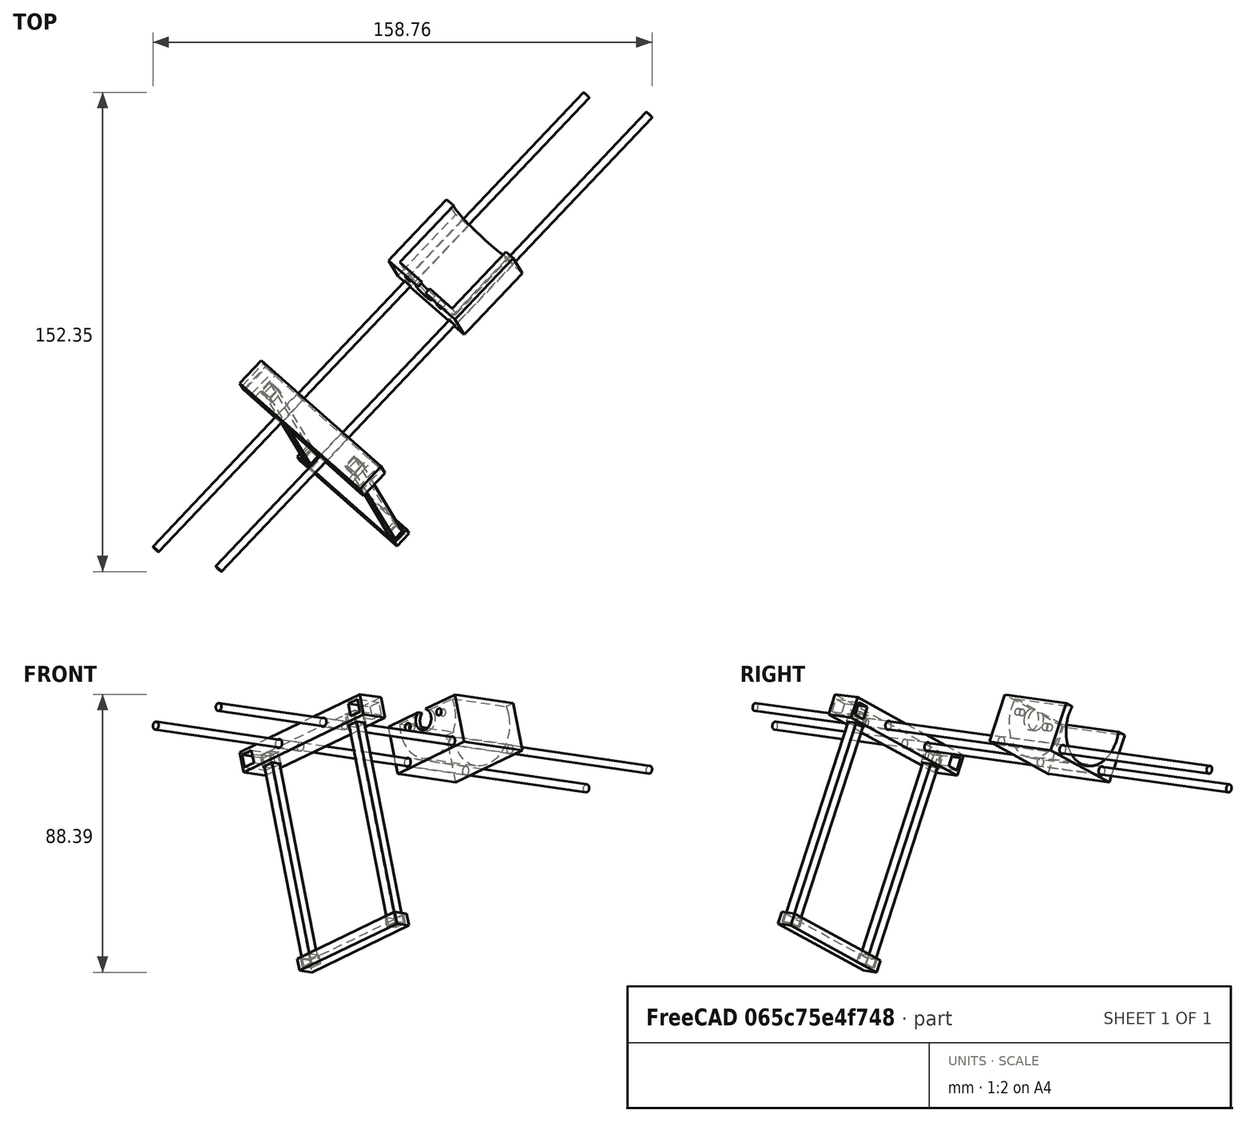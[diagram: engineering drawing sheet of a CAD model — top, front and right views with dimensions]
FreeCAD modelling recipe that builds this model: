
FCSTD DOCUMENT  (FreeCAD 0.19R24366 (Git))
Label: sailface_assembly_v1
License: All rights reserved
LicenseURL: http://en.wikipedia.org/wiki/All_rights_reserved
objects: Part::FeaturePython×53, App::FeaturePython×25, App::Link×10, App::MeasureDistance×1
note: 51 computed .brp shape members not serialized (recipe doc carries the construction recipe); baked Part::Feature solids carry a one-line shape summary decoded from their .brp
EXTERNAL_REF file=rudder_coarse_1.FCStd obj=Part
EXTERNAL_REF file=hulltest9.FCStd obj=Part
EXTERNAL_REF file=ServoSunFinderSF3218MG.FCStd obj=Part
EXTERNAL_REF file=Battery_VoltaicV70.FCStd obj=Part
EXTERNAL_REF file=internalstructure.FCStd obj=Assembly001
EXTERNAL_REF file=sailface_prop_motor_assembly.FCStd obj=Assembly001
EXTERNAL_REF file=ElectronicAssembly.FCStd obj=Part003

FEATURE [App::Link] Link  label="PartRudderWithPost"
  LinkPlacement = pos=(-220.039,-29.8961,-114.206) rot=(0.968596,0.172423,0.179146;1.79451rad)
  LinkedObject = -> <external rudder_coarse_1.FCStd>#Part
  Placement = pos=(-220.039,-29.8961,-114.206) rot=(0.968596,0.172423,0.179146;1.79451rad)
FEATURE [App::Link] Link002  label="Hull9"
  LinkPlacement = pos=(159.25,63.0194,-342.139) rot=(0.956231,-0.262504,0.12928;2.88979rad)
  LinkedObject = -> <external hulltest9.FCStd>#Part
  Placement = pos=(159.25,63.0194,-342.139) rot=(0.956231,-0.262504,0.12928;2.88979rad)
FEATURE [App::Link] Link003  label="Servo_SF3218MG001"
  LinkPlacement = pos=(50.6845,245.566,-385.314) rot=(0.448667,0.484449,-0.751004;2.6409rad)
  LinkedObject = -> <external ServoSunFinderSF3218MG.FCStd>#Part
  Placement = pos=(50.6845,245.566,-385.314) rot=(0.448667,0.484449,-0.751004;2.6409rad)
FEATURE [App::Link] Link012  label="PartBatteryVoltaicV071"
  LinkPlacement = pos=(257.834,77.0747,-229.776) rot=(0.318237,-0.762093,0.563861;1.78727rad)
  LinkedObject = -> <external Battery_VoltaicV70.FCStd>#Part
  Placement = pos=(257.834,77.0747,-229.776) rot=(0.318237,-0.762093,0.563861;1.78727rad)
FEATURE [App::Link] Link013  label="InternalHolder"
  LinkPlacement = pos=(53.3906,223.534,-322.627) rot=(-0.671245,-0.121056,-0.731283;2.04659rad)
  LinkedObject = -> <external internalstructure.FCStd>#Assembly001
  Placement = pos=(53.3906,223.534,-322.627) rot=(-0.671245,-0.121056,-0.731283;2.04659rad)
FEATURE [Part::FeaturePython] Parts  # WARN: FeaturePython — macro-defined, semantics opaque (R4)
  Group = -> [Link,Link003,Link013]
  GroupMode = 0
FEATURE [App::Link] Link015  label="InternalHolder001"
  LinkPlacement = pos=(36.7501,244.979,-385.283) rot=(0.56648,0.820791,0.073504;1.79616rad)
  LinkedObject = -> <external internalstructure.FCStd>#Assembly001
  Placement = pos=(36.7501,244.979,-385.283) rot=(0.56648,0.820791,0.073504;1.79616rad)
FEATURE [App::Link] Link016  label="PropMotorAssembly001"
  LinkPlacement = pos=(-323.878,337.344,47.3147) rot=(-0.16827,-0.265613,-0.949281;1.40405rad)
  LinkedObject = -> <external sailface_prop_motor_assembly.FCStd>#Assembly001
  Placement = pos=(-323.878,337.344,47.3147) rot=(-0.16827,-0.265613,-0.949281;1.40405rad)
FEATURE [App::Link] Link017  label="Servo_SF3218MG002"
  LinkPlacement = pos=(69.9259,133.783,-332.457) rot=(0.343106,0.929153,-0.137671;2.95548rad)
  LinkedObject = -> <external ServoSunFinderSF3218MG.FCStd>#Part
  Placement = pos=(69.9259,133.783,-332.457) rot=(0.343106,0.929153,-0.137671;2.95548rad)
FEATURE [App::Link] Link018  label="PartRudderWithPost001"
  LinkPlacement = pos=(-10.9166,185.291,-322.393) rot=(-0.886207,0.1344,-0.443367;1.71414rad)
  LinkedObject = -> <external rudder_coarse_1.FCStd>#Part
  Placement = pos=(-10.9166,185.291,-322.393) rot=(-0.886207,0.1344,-0.443367;1.71414rad)
FEATURE [App::MeasureDistance] Distance  label="Distance: 87.01 mm"
  Distance = 87.0115
  P1 = (104.997,143.854,-281.372)
  P2 = (50.1048,77.3799,-293.166)
FEATURE [App::Link] Link019  label="ElectronicsEnclosure"
  LinkedObject = -> <external ElectronicAssembly.FCStd>#Part003
FEATURE [Part::FeaturePython] Parts002  label="MasterAssemblyParts"  # WARN: FeaturePython — macro-defined, semantics opaque (R4)
  Group = -> [Link002,Link012,Link015,Link016,Link017,Link018,Link019]
  GroupMode = 0
FEATURE [Part::FeaturePython] Assembly  # WARN: FeaturePython — macro-defined, semantics opaque (R4)
  AutoRelax = true
  BuildShape = 0
  Freeze = true
  Group = -> [Constraints,Elements,Parts]
  Verbose = false
  _SolverType = 1
  _Version = 1
FEATURE [App::FeaturePython] Constraints  # WARN: FeaturePython — macro-defined, semantics opaque (R4)
  Group = -> [Constraint,Constraint006]
  _Version = 1
FEATURE [App::FeaturePython] Elements  # WARN: FeaturePython — macro-defined, semantics opaque (R4)
  Group = -> [_Element001,_Element003,_Element005,_Element008,_Element011,_Element012,_Element,_Element013,_Element014,_Element015,_Element016,_Element017,_Element018,_Element019,_Element020,_Element023,_Element025,_Element027,_Element029,_Element034,_Element035,_Element040,_Element041,_Element042]
FEATURE [Part::FeaturePython] _Element001  # link proxy (typed FeaturePython)
  Detach = false
  LinkTransform = true
  LinkedObject = -> Link002 [Extrude011.Face10]
  _Parent = -> Elements
FEATURE [Part::FeaturePython] _Element003  # link proxy (typed FeaturePython)
  Detach = false
  LinkTransform = true
  LinkedObject = -> Link002 [Extrude011.Face4]
  _Parent = -> Elements
FEATURE [Part::FeaturePython] _Element005  # link proxy (typed FeaturePython)
  Detach = false
  LinkTransform = true
  LinkedObject = -> Link002 [Extrude011.Face6]
  _Parent = -> Elements
FEATURE [Part::FeaturePython] _Element008  # link proxy (typed FeaturePython)
  Detach = false
  LinkTransform = true
  LinkedObject = -> Link003 [Solid.Face33]
  _Parent = -> Elements
FEATURE [Part::FeaturePython] _Element011  # link proxy (typed FeaturePython)
  Detach = false
  LinkTransform = true
  LinkedObject = -> Link003 [Solid.Face34]
  _Parent = -> Elements
FEATURE [Part::FeaturePython] _Element012  # link proxy (typed FeaturePython)
  Detach = false
  LinkTransform = true
  LinkedObject = -> Link003 [Solid.Face1]
  _Parent = -> Elements
FEATURE [Part::FeaturePython] _Element  # link proxy (typed FeaturePython)
  Detach = false
  LinkTransform = true
  LinkedObject = -> Link013 [1.$Element.]
  _Parent = -> Elements
FEATURE [Part::FeaturePython] _Element013  # link proxy (typed FeaturePython)
  Detach = false
  LinkTransform = true
  LinkedObject = -> Link012 [Pad001.Face2]
  _Parent = -> Elements
FEATURE [Part::FeaturePython] _Element014  # link proxy (typed FeaturePython)
  Detach = false
  LinkTransform = true
  LinkedObject = -> Link012 [Pad001.Face5]
  _Parent = -> Elements
FEATURE [Part::FeaturePython] _Element015  # link proxy (typed FeaturePython)
  Detach = false
  LinkTransform = true
  LinkedObject = -> Link013 [1.$Element001.]
  _Parent = -> Elements
FEATURE [App::FeaturePython] Constraint  label="PlaneAlignment001"  # WARN: FeaturePython — macro-defined, semantics opaque (R4)
  Angle = 0
  AnglePitch = 0
  AngleRoll = 0
  Cascade = false
  Disabled = false
  Group = -> [ElementLink,ElementLink011]
  LockAngle = false
  _ConstraintType = 37
  _Parent = -> Constraints
FEATURE [App::FeaturePython] ElementLink  label="_Element014"  # link proxy (typed FeaturePython)
  LinkTransform = true
  LinkedObject = -> _Element014
  _Parent = -> Constraint
FEATURE [App::FeaturePython] ElementLink011  label="_Element015"  # link proxy (typed FeaturePython)
  LinkTransform = true
  LinkedObject = -> _Element015
  _Parent = -> Constraint
FEATURE [Part::FeaturePython] _Element016  # link proxy (typed FeaturePython)
  Detach = false
  LinkTransform = true
  LinkedObject = -> Link013 [1.$Element002.]
  _Parent = -> Elements
FEATURE [Part::FeaturePython] _Element017  # link proxy (typed FeaturePython)
  Detach = false
  LinkTransform = true
  LinkedObject = -> Link013 [1.$Element003.]
  _Parent = -> Elements
FEATURE [Part::FeaturePython] _Element018  # link proxy (typed FeaturePython)
  Detach = false
  LinkTransform = true
  LinkedObject = -> Link013 [1.$Element004.]
  _Parent = -> Elements
FEATURE [Part::FeaturePython] _Element019  # link proxy (typed FeaturePython)
  Detach = false
  LinkTransform = true
  LinkedObject = -> Link003 [Solid.Face107]
  _Parent = -> Elements
FEATURE [App::FeaturePython] Constraint006  label="PlaneCoincident001"  # WARN: FeaturePython — macro-defined, semantics opaque (R4)
  Angle = 0
  AnglePitch = 0
  AngleRoll = 0
  Cascade = false
  Disabled = false
  Group = -> [ElementLink014,ElementLink015]
  LockAngle = false
  Multiply = false
  OffsetX = 0
  OffsetY = 0
  _ConstraintType = 35
  _Parent = -> Constraints
FEATURE [App::FeaturePython] ElementLink014  label="_Element012"  # link proxy (typed FeaturePython)
  LinkTransform = true
  LinkedObject = -> _Element012
  _Parent = -> Constraint006
FEATURE [App::FeaturePython] ElementLink015  label="_Element017"  # link proxy (typed FeaturePython)
  LinkTransform = true
  LinkedObject = -> _Element017
  _Parent = -> Constraint006
FEATURE [Part::FeaturePython] _Element020  # link proxy (typed FeaturePython)
  Detach = false
  LinkTransform = true
  LinkedObject = -> Link013 [1.$Element005.]
  _Parent = -> Elements
FEATURE [Part::FeaturePython] _Element023  # link proxy (typed FeaturePython)
  Detach = false
  LinkTransform = true
  LinkedObject = -> Link013 [1.$Element006.]
  _Parent = -> Elements
FEATURE [Part::FeaturePython] _Element025  # link proxy (typed FeaturePython)
  Detach = false
  LinkTransform = true
  LinkedObject = -> Link013 [1.$Element007.]
  _Parent = -> Elements
FEATURE [Part::FeaturePython] _Element027  # link proxy (typed FeaturePython)
  Detach = false
  LinkTransform = true
  LinkedObject = -> Link013 [1.$Element008.]
  _Parent = -> Elements
FEATURE [Part::FeaturePython] _Element029  # link proxy (typed FeaturePython)
  Detach = false
  LinkTransform = true
  LinkedObject = -> Link013 [1.$Element009.]
  _Parent = -> Elements
FEATURE [Part::FeaturePython] _Element034  # link proxy (typed FeaturePython)
  Detach = false
  LinkTransform = true
  LinkedObject = -> Link013 [1.$Element010.]
  _Parent = -> Elements
FEATURE [Part::FeaturePython] _Element035  # link proxy (typed FeaturePython)
  Detach = false
  LinkTransform = true
  LinkedObject = -> Link013 [1.$Element011.]
  _Parent = -> Elements
FEATURE [Part::FeaturePython] _Element040  # link proxy (typed FeaturePython)
  Detach = false
  LinkTransform = true
  LinkedObject = -> Link013 [1.$_Element061.]
  _Parent = -> Elements
FEATURE [Part::FeaturePython] _Element041  # link proxy (typed FeaturePython)
  Detach = false
  LinkTransform = true
  LinkedObject = -> Link002 [Compound.Face4]
  _Parent = -> Elements
FEATURE [Part::FeaturePython] _Element042  # link proxy (typed FeaturePython)
  Detach = false
  LinkTransform = true
  LinkedObject = -> Link013 [1.$Element012.]
  _Parent = -> Elements
FEATURE [Part::FeaturePython] Assembly002  label="MasterAssembly"  # WARN: FeaturePython — macro-defined, semantics opaque (R4)
  AutoRelax = true
  BuildShape = 0
  Freeze = false
  Group = -> [Constraints002,Elements002,Parts002]
  Verbose = false
  _SolverType = 1
  _Version = 1
FEATURE [App::FeaturePython] Constraints002  # WARN: FeaturePython — macro-defined, semantics opaque (R4)
  Group = -> [Constraint007,Constraint008,Constraint009,Constraint010,Constraint011]
  _Version = 1
FEATURE [App::FeaturePython] Elements002  label="MasterAssemblyElements"  # WARN: FeaturePython — macro-defined, semantics opaque (R4)
  Group = -> [_Element043,_Element044,_Element045,_Element046,_Element047,_Element048,_Element049,_Element050,_Element051,_Element052,_Element053,_Element054,_Element055,_Element056,_Element057,_Element058,_Element059,_Element060,_Element061,_Element062,_Element063,_Element064,_Element065,_Element066,_Element067]
FEATURE [Part::FeaturePython] _Element043  # link proxy (typed FeaturePython)
  Detach = false
  LinkTransform = true
  LinkedObject = -> Link015 [1.$Element013.]
  _Parent = -> Elements002
FEATURE [Part::FeaturePython] _Element044  # link proxy (typed FeaturePython)
  Detach = false
  LinkTransform = true
  LinkedObject = -> Link002 [Extrude011.Face18]
  _Parent = -> Elements002
FEATURE [Part::FeaturePython] _Element045  # link proxy (typed FeaturePython)
  Detach = false
  LinkTransform = true
  LinkedObject = -> Link015 [1.$_Element064.]
  _Parent = -> Elements002
FEATURE [Part::FeaturePython] _Element046  # link proxy (typed FeaturePython)
  Detach = false
  LinkTransform = true
  LinkedObject = -> Link002 [Compound.Face4]
  _Parent = -> Elements002
FEATURE [App::FeaturePython] Constraint007  label="PlaneCoincident"  # WARN: FeaturePython — macro-defined, semantics opaque (R4)
  Angle = 0
  AnglePitch = 0
  AngleRoll = 0
  Cascade = false
  Disabled = false
  Group = -> [ElementLink016,ElementLink017]
  LockAngle = false
  Multiply = false
  OffsetX = 0
  OffsetY = 0
  _ConstraintType = 35
  _Parent = -> Constraints002
FEATURE [App::FeaturePython] ElementLink016  label="_Element043"  # link proxy (typed FeaturePython)
  LinkTransform = true
  LinkedObject = -> _Element043
  _Parent = -> Constraint007
FEATURE [App::FeaturePython] ElementLink017  label="_Element044"  # link proxy (typed FeaturePython)
  LinkTransform = true
  LinkedObject = -> _Element044
  _Parent = -> Constraint007
FEATURE [Part::FeaturePython] _Element047  # link proxy (typed FeaturePython)
  Detach = false
  LinkTransform = true
  LinkedObject = -> Link015 [1.$Element014.]
  _Parent = -> Elements002
FEATURE [Part::FeaturePython] _Element048  # link proxy (typed FeaturePython)
  Detach = false
  LinkTransform = true
  LinkedObject = -> Link015 [1.$Element015.]
  _Parent = -> Elements002
FEATURE [Part::FeaturePython] _Element049  # link proxy (typed FeaturePython)
  Detach = false
  LinkTransform = true
  LinkedObject = -> Link015 [1.$Element011.]
  _Parent = -> Elements002
FEATURE [Part::FeaturePython] _Element050  # link proxy (typed FeaturePython)
  Detach = false
  LinkTransform = true
  LinkedObject = -> Link015 [1.$Element016.]
  _Parent = -> Elements002
FEATURE [Part::FeaturePython] _Element051  # link proxy (typed FeaturePython)
  Detach = false
  LinkTransform = true
  LinkedObject = -> Link016 [1.$Element.]
  _Parent = -> Elements002
FEATURE [Part::FeaturePython] _Element052  # link proxy (typed FeaturePython)
  Detach = false
  LinkTransform = true
  LinkedObject = -> Link015 [1.$Element006.]
  _Parent = -> Elements002
FEATURE [Part::FeaturePython] _Element053  # link proxy (typed FeaturePython)
  Detach = false
  LinkTransform = true
  LinkedObject = -> Link016 [1.$Element001.]
  _Parent = -> Elements002
FEATURE [Part::FeaturePython] _Element054  # link proxy (typed FeaturePython)
  Detach = false
  LinkTransform = true
  LinkedObject = -> Link015 [1.$Element007.]
  _Parent = -> Elements002
FEATURE [Part::FeaturePython] _Element055  # link proxy (typed FeaturePython)
  Detach = false
  LinkTransform = true
  LinkedObject = -> Link016 [1.$Element002.]
  _Parent = -> Elements002
FEATURE [Part::FeaturePython] _Element056  # link proxy (typed FeaturePython)
  Detach = false
  LinkTransform = true
  LinkedObject = -> Link016 [1.$Element003.]
  _Parent = -> Elements002
FEATURE [Part::FeaturePython] _Element057  # link proxy (typed FeaturePython)
  Detach = false
  LinkTransform = true
  LinkedObject = -> Link015 [1.$Element008.]
  _Parent = -> Elements002
FEATURE [Part::FeaturePython] _Element058  # link proxy (typed FeaturePython)
  Detach = false
  LinkTransform = true
  LinkedObject = -> Link016 [1.$Element004.]
  _Parent = -> Elements002
FEATURE [Part::FeaturePython] _Element059  # link proxy (typed FeaturePython)
  Detach = false
  LinkTransform = true
  LinkedObject = -> Link015 [1.$Element009.]
  _Parent = -> Elements002
FEATURE [App::FeaturePython] Constraint008  label="AxialAlignment"  # WARN: FeaturePython — macro-defined, semantics opaque (R4)
  Angle = 0
  AnglePitch = 0
  AngleRoll = 0
  Disabled = false
  Group = -> [ElementLink018,ElementLink019]
  LockAngle = false
  Multiply = false
  _ConstraintType = 36
  _Parent = -> Constraints002
FEATURE [App::FeaturePython] ElementLink018  label="_Element052"  # link proxy (typed FeaturePython)
  LinkTransform = true
  LinkedObject = -> _Element052
  _Parent = -> Constraint008
FEATURE [App::FeaturePython] ElementLink019  label="_Element051"  # link proxy (typed FeaturePython)
  LinkTransform = true
  LinkedObject = -> _Element051
  _Parent = -> Constraint008
FEATURE [Part::FeaturePython] _Element060  # link proxy (typed FeaturePython)
  Detach = false
  LinkTransform = true
  LinkedObject = -> Link015 [1.$Element017.]
  _Parent = -> Elements002
FEATURE [Part::FeaturePython] _Element061  # link proxy (typed FeaturePython)
  Detach = false
  LinkTransform = true
  LinkedObject = -> Link012 [Pad001.Face2]
  _Parent = -> Elements002
FEATURE [Part::FeaturePython] _Element062  # link proxy (typed FeaturePython)
  Detach = false
  LinkTransform = true
  LinkedObject = -> Link015 [1.$Element001.]
  _Parent = -> Elements002
FEATURE [Part::FeaturePython] _Element063  # link proxy (typed FeaturePython)
  Detach = false
  LinkTransform = true
  LinkedObject = -> Link012 [Pad001.Face4]
  _Parent = -> Elements002
FEATURE [Part::FeaturePython] _Element064  # link proxy (typed FeaturePython)
  Detach = false
  LinkTransform = true
  LinkedObject = -> Link012 [Pad001.Face1]
  _Parent = -> Elements002
FEATURE [Part::FeaturePython] _Element065  # link proxy (typed FeaturePython)
  Detach = false
  LinkTransform = true
  LinkedObject = -> Link015 [1.$Element018.]
  _Parent = -> Elements002
FEATURE [Part::FeaturePython] _Element066  # link proxy (typed FeaturePython)
  Detach = false
  LinkTransform = true
  LinkedObject = -> Link012 [Pad001.Face3]
  _Parent = -> Elements002
FEATURE [Part::FeaturePython] _Element067  # link proxy (typed FeaturePython)
  Detach = false
  LinkTransform = true
  LinkedObject = -> Link015 [1.$Element.]
  _Parent = -> Elements002
FEATURE [App::FeaturePython] Constraint009  label="MultiParallel"  # WARN: FeaturePython — macro-defined, semantics opaque (R4)
  Angle = 0
  AnglePitch = 0
  AngleRoll = 0
  Disabled = false
  Group = -> [ElementLink020,ElementLink021]
  LockAngle = false
  _ConstraintType = 291
  _Parent = -> Constraints002
FEATURE [App::FeaturePython] ElementLink020  label="_Element061"  # link proxy (typed FeaturePython)
  LinkTransform = true
  LinkedObject = -> _Element061
  _Parent = -> Constraint009
FEATURE [App::FeaturePython] ElementLink021  label="_Element060"  # link proxy (typed FeaturePython)
  LinkTransform = true
  LinkedObject = -> _Element060
  _Parent = -> Constraint009
FEATURE [App::FeaturePython] Constraint010  label="PlaneAlignment"  # WARN: FeaturePython — macro-defined, semantics opaque (R4)
  Angle = 0
  AnglePitch = 0
  AngleRoll = 0
  Cascade = false
  Disabled = false
  Group = -> [ElementLink022,ElementLink023]
  LockAngle = false
  _ConstraintType = 37
  _Parent = -> Constraints002
FEATURE [App::FeaturePython] ElementLink022  label="_Element064"  # link proxy (typed FeaturePython)
  LinkTransform = true
  LinkedObject = -> _Element064
  _Parent = -> Constraint010
FEATURE [App::FeaturePython] ElementLink023  label="_Element065"  # link proxy (typed FeaturePython)
  LinkTransform = true
  LinkedObject = -> _Element065
  _Parent = -> Constraint010
FEATURE [App::FeaturePython] Constraint011  label="PlaneAlignment002"  # WARN: FeaturePython — macro-defined, semantics opaque (R4)
  Angle = 0
  AnglePitch = 0
  AngleRoll = 0
  Cascade = false
  Disabled = false
  Group = -> [ElementLink024,ElementLink025]
  LockAngle = false
  _ConstraintType = 37
  _Parent = -> Constraints002
FEATURE [App::FeaturePython] ElementLink024  label="_Element063"  # link proxy (typed FeaturePython)
  LinkTransform = true
  LinkedObject = -> _Element063
  _Parent = -> Constraint011
FEATURE [App::FeaturePython] ElementLink025  label="_Element062"  # link proxy (typed FeaturePython)
  LinkTransform = true
  LinkedObject = -> _Element062
  _Parent = -> Constraint011

RESOLVED EXTERNAL PARTS (link-assembly join: the EXTERNAL_REF files above that resolve inside this repo's crawl, each included once):
---- part ServoSunFinderSF3218MG.FCStd = doc fcstd_3688cb63020c ----
FCSTD DOCUMENT  (FreeCAD 0.19R24366 (Git))
Label: ServoSunFinderSF3218MG
License: All rights reserved
LicenseURL: http://en.wikipedia.org/wiki/All_rights_reserved
objects: Sketcher::SketchObject×15, PartDesign::Pad×10, PartDesign::Pocket×5, App::Part×5, PartDesign::Body×4, Part::Feature×2, Mesh::Feature×1
note: 51 computed .brp shape members not serialized (recipe doc carries the construction recipe); baked Part::Feature solids carry a one-line shape summary decoded from their .brp

FEATURE [Part::Feature] Solid  label="Servo_SF3218MG"
  Placement = pos=(0,0,0) rot=(1,0,0;1.5708rad)
  shape: bbox 20 x 62.45 x 46.03 mm, 436 faces (baked)
FEATURE [Sketcher::SketchObject] Sketch  label="ServoHolder"
  FullyConstrained = false
  MapMode = 4
  Placement = pos=(0,0,0) rot=(0.57735,0.57735,0.57735;2.0944rad)
  sketch-geometry (8):
    g0: LineSegment StartX=-27.0989 StartY=-22.5482 StartZ=0 EndX=27.4011 EndY=-22.5482 EndZ=0
    g1: LineSegment StartX=20.6511 StartY=-19.5482 StartZ=0 EndX=20.6511 EndY=8.45178 EndZ=0
    g2: LineSegment StartX=20.6511 StartY=8.45178 StartZ=0 EndX=27.4011 EndY=8.45178 EndZ=0
    g3: LineSegment StartX=-20.3489 StartY=-19.5482 StartZ=0 EndX=-20.3489 EndY=8.45178 EndZ=0
    g4: LineSegment StartX=-20.3489 StartY=8.45178 StartZ=0 EndX=-27.0989 EndY=8.45178 EndZ=0
    g5: LineSegment StartX=20.6511 StartY=-19.5482 StartZ=0 EndX=-20.3489 EndY=-19.5482 EndZ=0
    g6: LineSegment StartX=-27.0989 StartY=8.45178 StartZ=0 EndX=-27.0989 EndY=-22.5482 EndZ=0
    g7: LineSegment StartX=27.4011 StartY=8.45178 StartZ=0 EndX=27.4011 EndY=-22.5482 EndZ=0
  constraints (22):
    c: Horizontal(g0)
    c: Coincident(g1,g2)
    c: Horizontal(g2)
    c: Vertical(g1)
    c: Coincident(g3,g4)
    c: Horizontal(g4)
    c: Vertical(g3)
    c: Coincident(g5,g1)
    c: Coincident(g5,g3)
    c: Horizontal(g5)
    c: Coincident(g6,g4)
    c: Coincident(g6,g0)
    c: Vertical(g6)
    c: Coincident(g7,g2)
    c: Coincident(g7,g0)
    c: Vertical(g7)
    c: DistanceX(g0,g0) = 54.5
    c: DistanceX(g5,g5) = 41
    c: Equal(g4,g2)
    c: Horizontal(g3,g1)
    c: DistanceY(g0,g1) = 3
    c: DistanceY(g1,g1) = 28
FEATURE [Sketcher::SketchObject] Sketch001  label="WireHoleSketch"
  FullyConstrained = false
  Placement = pos=(0,27.4011,0) rot=(0,0.707107,0.707107;3.14159rad)
  sketch-geometry (4):
    g0: LineSegment StartX=-5.36505 StartY=-10.7623 StartZ=0 EndX=-14.3651 EndY=-10.7623 EndZ=0
    g1: LineSegment StartX=-14.3651 StartY=-10.7623 StartZ=0 EndX=-14.3651 EndY=-16.7623 EndZ=0
    g2: LineSegment StartX=-14.3651 StartY=-16.7623 StartZ=0 EndX=-5.36505 EndY=-16.7623 EndZ=0
    g3: LineSegment StartX=-5.36505 StartY=-16.7623 StartZ=0 EndX=-5.36505 EndY=-10.7623 EndZ=0
  constraints (10):
    c: Coincident(g1,g2)
    c: Coincident(g2,g3)
    c: Coincident(g3,g0)
    c: Horizontal(g0)
    c: Horizontal(g2)
    c: Vertical(g1)
    c: Vertical(g3)
    c: Coincident(g1,g0)
    c: DistanceX(g0,g0) = 9
    c: DistanceY(g1,g1) = 6
FEATURE [PartDesign::Pad] Pad  label="ExtrudeServoHolder"
  Direction = (1,1,1)
  Length = 20
  Length2 = 100
  Placement = pos=(0,0,0) rot=(0.57735,0.57735,0.57735;2.0944rad)
  Profile = -> Sketch
  Type = 0
FEATURE [PartDesign::Pocket] Pocket
  BaseFeature = -> Pad
  Length = 8
  Length2 = 100
  Placement = pos=(0,0,0) rot=(0.57735,0.57735,0.57735;2.0944rad)
  Profile = -> Sketch001
  Type = 0
FEATURE [PartDesign::Body] Body
  Group = -> [Sketch001,Sketch,Pad,Pocket]
  Origin = -> Origin001
  Tip = -> Pocket
FEATURE [App::Part] Part  label="Servo_SF3218MG001"
  Group = -> [Solid,Body]
  Origin = -> Origin
FEATURE [Sketcher::SketchObject] Sketch002  label="ServoHolder002"
  FullyConstrained = false
  MapMode = 4
  Placement = pos=(0,0,0) rot=(0.57735,0.57735,0.57735;2.0944rad)
  sketch-geometry (8):
    g0: LineSegment StartX=-27.0989 StartY=-22.5482 StartZ=0 EndX=27.4011 EndY=-22.5482 EndZ=0
    g1: LineSegment StartX=20.6511 StartY=-19.5482 StartZ=0 EndX=20.6511 EndY=8.45178 EndZ=0
    g2: LineSegment StartX=20.6511 StartY=8.45178 StartZ=0 EndX=27.4011 EndY=8.45178 EndZ=0
    g3: LineSegment StartX=-20.3489 StartY=-19.5482 StartZ=0 EndX=-20.3489 EndY=8.45178 EndZ=0
    g4: LineSegment StartX=-20.3489 StartY=8.45178 StartZ=0 EndX=-27.0989 EndY=8.45178 EndZ=0
    g5: LineSegment StartX=20.6511 StartY=-19.5482 StartZ=0 EndX=-20.3489 EndY=-19.5482 EndZ=0
    g6: LineSegment StartX=-27.0989 StartY=8.45178 StartZ=0 EndX=-27.0989 EndY=-22.5482 EndZ=0
    g7: LineSegment StartX=27.4011 StartY=8.45178 StartZ=0 EndX=27.4011 EndY=-22.5482 EndZ=0
  constraints (22):
    c: Horizontal(g0)
    c: Coincident(g1,g2)
    c: Horizontal(g2)
    c: Vertical(g1)
    c: Coincident(g3,g4)
    c: Horizontal(g4)
    c: Vertical(g3)
    c: Coincident(g5,g1)
    c: Coincident(g5,g3)
    c: Horizontal(g5)
    c: Coincident(g6,g4)
    c: Coincident(g6,g0)
    c: Vertical(g6)
    c: Coincident(g7,g2)
    c: Coincident(g7,g0)
    c: Vertical(g7)
    c: DistanceX(g0,g0) = 54.5
    c: DistanceX(g5,g5) = 41
    c: Equal(g4,g2)
    c: Horizontal(g3,g1)
    c: DistanceY(g0,g1) = 3
    c: DistanceY(g1,g1) = 28
FEATURE [PartDesign::Pad] Pad001  label="ExtrudeServoHolder001"
  Direction = (1,1,1)
  Length = 20
  Length2 = 100
  Placement = pos=(0,0,0) rot=(0.57735,0.57735,0.57735;2.0944rad)
  Profile = -> Sketch002
  Type = 0
FEATURE [Sketcher::SketchObject] Sketch004  label="WireHoleSketch001"
  FullyConstrained = false
  Placement = pos=(0,27.4011,0) rot=(0,0.707107,0.707107;3.14159rad)
  sketch-geometry (4):
    g0: LineSegment StartX=-5.36505 StartY=-10.7623 StartZ=0 EndX=-14.3651 EndY=-10.7623 EndZ=0
    g1: LineSegment StartX=-14.3651 StartY=-10.7623 StartZ=0 EndX=-14.3651 EndY=-16.7623 EndZ=0
    g2: LineSegment StartX=-14.3651 StartY=-16.7623 StartZ=0 EndX=-5.36505 EndY=-16.7623 EndZ=0
    g3: LineSegment StartX=-5.36505 StartY=-16.7623 StartZ=0 EndX=-5.36505 EndY=-10.7623 EndZ=0
  constraints (10):
    c: Coincident(g1,g2)
    c: Coincident(g2,g3)
    c: Coincident(g3,g0)
    c: Horizontal(g0)
    c: Horizontal(g2)
    c: Vertical(g1)
    c: Vertical(g3)
    c: Coincident(g1,g0)
    c: DistanceX(g0,g0) = 9
    c: DistanceY(g1,g1) = 6
FEATURE [PartDesign::Pocket] Pocket001  label="ServoHolder001"
  BaseFeature = -> Pad001
  Length = 8
  Length2 = 100
  Placement = pos=(0,0,0) rot=(0.57735,0.57735,0.57735;2.0944rad)
  Profile = -> Sketch004
  Type = 0
FEATURE [Sketcher::SketchObject] Sketch003  label="HorizontalSupportHole"
  FullyConstrained = false
  MapMode = 5
  Placement = pos=(0,0,0) rot=(0.57735,0.57735,-0.57735;4.18879rad)
  Support = -> [Pocket001]
  sketch-geometry (8):
    g0: LineSegment StartX=-21.0477 StartY=17.881 StartZ=0 EndX=-26.2545 EndY=17.881 EndZ=0
    g1: LineSegment StartX=-26.2545 StartY=17.881 StartZ=0 EndX=-26.2545 EndY=22.4547 EndZ=0
    g2: LineSegment StartX=26.9512 StartY=17.881 StartZ=0 EndX=21.7444 EndY=17.881 EndZ=0
    g3: LineSegment StartX=26.9512 StartY=22.4547 StartZ=0 EndX=26.9512 EndY=17.881 EndZ=0
    g4: LineSegment StartX=21.7444 StartY=19.7543 StartZ=0 EndX=21.7444 EndY=17.881 EndZ=0
    g5: LineSegment StartX=-21.0477 StartY=17.881 StartZ=0 EndX=-21.0477 EndY=19.7543 EndZ=0
    g6: LineSegment StartX=-21.0477 StartY=19.7543 StartZ=0 EndX=21.7444 EndY=19.7543 EndZ=0
    g7: LineSegment StartX=-26.2545 StartY=22.4547 StartZ=0 EndX=26.9512 EndY=22.4547 EndZ=0
  constraints (18):
    c: Coincident(g0,g1)
    c: Horizontal(g0)
    c: Vertical(g1)
    c: Coincident(g3,g2)
    c: Horizontal(g2)
    c: Vertical(g3)
    c: Coincident(g4,g2)
    c: Coincident(g6,g5)
    c: Coincident(g6,g4)
    c: Horizontal(g6)
    c: Coincident(g1,g7)
    c: Horizontal(g7)
    c: Coincident(g3,g7)
    c: Equal(g3,g1)
    c: Equal(g0,g2)
    c: Coincident(g0,g5)
    c: Vertical(g5)
    c: Vertical(g4)
FEATURE [Part::Feature] Solid001  label="ServoHorn"
  shape: bbox 34.33 x 14.81 x 6 mm, 52 faces (baked)
FEATURE [App::Part] Part002  label="ServoHorn001"
  Group = -> [Solid001]
  Origin = -> Origin004
FEATURE [Sketcher::SketchObject] Sketch007
  FullyConstrained = true
  MapMode = 5
  Support = -> [XY_Plane006]
  sketch-geometry (1):
    g0: Circle CenterX=0 CenterY=0 CenterZ=0 NormalX=0 NormalY=0 NormalZ=1 AngleXU=0 Radius=2.5
  constraints (2):
    c: Coincident(g0,g-1)
    c: Diameter(g0) = 5
FEATURE [PartDesign::Pad] Pad002
  Direction = (1,1,1)
  Length = 50
  Length2 = 100
  Profile = -> Sketch007
  Type = 0
FEATURE [Sketcher::SketchObject] Sketch008
  FullyConstrained = true
  MapMode = 5
  Placement = pos=(0,0,50) rot=(0,0,1;0rad)
  Support = -> [Pad002]
  sketch-geometry (1):
    g0: Circle CenterX=0 CenterY=0 CenterZ=0 NormalX=0 NormalY=0 NormalZ=1 AngleXU=0 Radius=1.5
  constraints (2):
    c: Coincident(g0,g-1)
    c: Diameter(g0) = 3
FEATURE [PartDesign::Pocket] Pocket003
  BaseFeature = -> Pad002
  Length = 75
  Length2 = 100
  Profile = -> Sketch008
  Type = 0
FEATURE [PartDesign::Body] Body002
  Group = -> [Sketch007,Pad002,Sketch008,Pocket003]
  Origin = -> Origin006
  Tip = -> Pocket003
FEATURE [App::Part] Part003  label="PostHoleJacket"
  Group = -> [Body002]
  Origin = -> Origin005
FEATURE [Sketcher::SketchObject] Sketch009
  FullyConstrained = true
  MapMode = 5
  Support = -> [XY_Plane008]
  sketch-geometry (4):
    g0: LineSegment StartX=0 StartY=0 StartZ=0 EndX=-54.5 EndY=0 EndZ=0
    g1: LineSegment StartX=-54.5 StartY=0 StartZ=0 EndX=-54.5 EndY=15 EndZ=0
    g2: LineSegment StartX=-54.5 StartY=15 StartZ=0 EndX=0 EndY=15 EndZ=0
    g3: LineSegment StartX=0 StartY=15 StartZ=0 EndX=0 EndY=0 EndZ=0
  constraints (11):
    c: Coincident(g0,g1)
    c: Coincident(g1,g2)
    c: Coincident(g2,g3)
    c: Coincident(g3,g0)
    c: Horizontal(g0)
    c: Horizontal(g2)
    c: Vertical(g1)
    c: Vertical(g3)
    c: Coincident(g0,g-1)
    c: DistanceX(g0,g0) = 54.5
    c: DistanceY(g1,g1) = 15
FEATURE [PartDesign::Pad] Pad003
  Direction = (1,1,1)
  Length = 14
  Length2 = 100
  Profile = -> Sketch009
  Type = 0
FEATURE [Sketcher::SketchObject] Sketch011
  ExternalGeometry = -> [Pad003]
  FullyConstrained = true
  MapMode = 5
  Placement = pos=(0,15,0) rot=(0,0.707107,0.707107;3.14159rad)
  Support = -> [Pad003]
  sketch-geometry (3):
    g0: Circle CenterX=27.25 CenterY=7 CenterZ=0 NormalX=0 NormalY=0 NormalZ=1 AngleXU=0 Radius=5
    g1: LineSegment StartX=27.25 StartY=7 StartZ=0 EndX=0 EndY=7 EndZ=0
    g2: LineSegment StartX=27.25 StartY=7 StartZ=0 EndX=54.5 EndY=7 EndZ=0
  constraints (9):
    c: Diameter(g0) = 10
    c: Coincident(g1,g0)
    c: PointOnObject(g1,g-5)
    c: Horizontal(g1)
    c: Coincident(g2,g0)
    c: PointOnObject(g2,g-4)
    c: Horizontal(g2)
    c: Equal(g1,g2)
    c: DistanceY(g0,g-4) = 7
FEATURE [PartDesign::Pad] Pad005
  BaseFeature = -> Pad003
  Direction = (1,1,1)
  Length = 10
  Length2 = 100
  Profile = -> Sketch011
  Type = 0
FEATURE [Mesh::Feature] Mesh  label="ServoHolderPart (Meshed)"
FEATURE [Sketcher::SketchObject] Sketch012
  ExternalGeometry = -> [Pad005]
  FullyConstrained = true
  MapMode = 5
  Placement = pos=(3e-15,25,-5.1e-15) rot=(0,0.707107,0.707107;3.14159rad)
  Support = -> [Pad005]
  sketch-geometry (1):
    g0: Circle CenterX=27.25 CenterY=7 CenterZ=0 NormalX=0 NormalY=0 NormalZ=1 AngleXU=0 Radius=3.4
  constraints (2):
    c: Coincident(g0,g-3)
    c: Diameter(g0) = 6.8
FEATURE [PartDesign::Pocket] Pocket004
  BaseFeature = -> Pad005
  Length = 30
  Length2 = 100
  Profile = -> Sketch012
  Type = 0
FEATURE [PartDesign::Body] Body003
  Group = -> [Sketch009,Pad003,Sketch011,Pad005,Sketch012,Pocket004]
  Origin = -> Origin008
  Tip = -> Pocket004
FEATURE [App::Part] Part004  label="ServoRudderHolderConnect"
  Group = -> [Body003]
  Origin = -> Origin007
FEATURE [PartDesign::Pad] Pad006
  BaseFeature = -> Pocket001
  Direction = (1,1,1)
  Length = 50
  Length2 = 100
  Placement = pos=(0,0,0) rot=(0.57735,0.57735,0.57735;2.0944rad)
  Profile = -> Sketch003
  Type = 0
FEATURE [Sketcher::SketchObject] Sketch013
  ExternalGeometry = -> [Pad006]
  FullyConstrained = false
  MapMode = 5
  Placement = pos=(-50,1.11e-14,0) rot=(-0.57735,-0.57735,0.57735;2.0944rad)
  Support = -> [Pad006]
  sketch-geometry (4):
    g0: LineSegment StartX=-27.0989 StartY=22.5482 StartZ=0 EndX=27.4011 EndY=22.5482 EndZ=0
    g1: LineSegment StartX=27.4011 StartY=22.5482 StartZ=0 EndX=27.4011 EndY=12.4768 EndZ=0
    g2: LineSegment StartX=27.4011 StartY=12.4768 StartZ=0 EndX=-27.0989 EndY=12.4768 EndZ=0
    g3: LineSegment StartX=-27.0989 StartY=12.4768 StartZ=0 EndX=-27.0989 EndY=22.5482 EndZ=0
  constraints (9):
    c: Coincident(g0,g1)
    c: Coincident(g1,g2)
    c: Coincident(g2,g3)
    c: Coincident(g3,g0)
    c: Horizontal(g2)
    c: Vertical(g1)
    c: Vertical(g3)
    c: Coincident(g0,g-4)
    c: Coincident(g-3,g0)
FEATURE [PartDesign::Pad] Pad007
  BaseFeature = -> Pad006
  Direction = (1,1,1)
  Length = 20
  Length2 = 100
  Placement = pos=(0,0,0) rot=(0.57735,0.57735,0.57735;2.0944rad)
  Profile = -> Sketch013
  Type = 0
FEATURE [Sketcher::SketchObject] Sketch014
  ExternalGeometry = -> [Pad007]
  FullyConstrained = true
  MapMode = 5
  Placement = pos=(1.4e-15,-4.2e-15,-12.4768) rot=(0,0,-1;1.5708rad)
  Support = -> [Pad007]
  sketch-geometry (5):
    g0: Circle CenterX=-0.151063 CenterY=-60 CenterZ=0 NormalX=0 NormalY=0 NormalZ=1 AngleXU=0 Radius=5
    g1: LineSegment StartX=-27.4011 StartY=-60 StartZ=0 EndX=-0.151063 EndY=-60 EndZ=0
    g2: LineSegment StartX=-0.151063 StartY=-60 StartZ=0 EndX=27.0989 EndY=-60 EndZ=0
    g3: LineSegment StartX=-0.151063 StartY=-50 StartZ=0 EndX=-0.151063 EndY=-60 EndZ=0
    g4: LineSegment StartX=-0.151063 StartY=-60 StartZ=0 EndX=-0.151063 EndY=-70 EndZ=0
  constraints (15):
    c: PointOnObject(g1,g-4)
    c: Horizontal(g1)
    c: Coincident(g2,g1)
    c: PointOnObject(g2,g-3)
    c: Horizontal(g2)
    c: Coincident(g0,g1)
    c: Equal(g2,g1)
    c: PointOnObject(g3,g-5)
    c: Coincident(g3,g0)
    c: PointOnObject(g4,g-6)
    c: Vertical(g4)
    c: Equal(g4,g3)
    c: Coincident(g4,g0)
    c: Vertical(g3)
    c: Radius(g0) = 5
FEATURE [PartDesign::Pad] Pad008
  BaseFeature = -> Pad007
  Direction = (1,1,1)
  Length = 10
  Length2 = 100
  Placement = pos=(0,0,0) rot=(0.57735,0.57735,0.57735;2.0944rad)
  Profile = -> Sketch014
  Type = 0
FEATURE [Sketcher::SketchObject] Sketch015
  ExternalGeometry = -> [Pad008]
  FullyConstrained = true
  MapMode = 5
  Placement = pos=(1.1e-15,-9e-16,-2.47682) rot=(0,0,-1;1.5708rad)
  Support = -> [Pad008]
  sketch-geometry (1):
    g0: Circle CenterX=-0.151063 CenterY=-60 CenterZ=0 NormalX=0 NormalY=0 NormalZ=1 AngleXU=0 Radius=3.4
  constraints (2):
    c: Coincident(g0,g-3)
    c: Diameter(g0) = 6.8
FEATURE [PartDesign::Pocket] Pocket005
  BaseFeature = -> Pad008
  Length = 25
  Length2 = 100
  Placement = pos=(0,0,0) rot=(0.57735,0.57735,0.57735;2.0944rad)
  Profile = -> Sketch015
  Type = 0
FEATURE [Sketcher::SketchObject] Sketch016
  ExternalGeometry = -> [Pocket005]
  FullyConstrained = true
  MapMode = 5
  Placement = pos=(20,-1.78e-14,0) rot=(0.57735,0.57735,0.57735;2.0944rad)
  Support = -> [Pocket005]
  sketch-geometry (4):
    g0: LineSegment StartX=-27.0989 StartY=-22.5482 StartZ=0 EndX=27.4011 EndY=-22.5482 EndZ=0
    g1: LineSegment StartX=27.4011 StartY=-22.5482 StartZ=0 EndX=27.4011 EndY=-17.5482 EndZ=0
    g2: LineSegment StartX=27.4011 StartY=-17.5482 StartZ=0 EndX=-27.0989 EndY=-17.5482 EndZ=0
    g3: LineSegment StartX=-27.0989 StartY=-17.5482 StartZ=0 EndX=-27.0989 EndY=-22.5482 EndZ=0
  constraints (11):
    c: Coincident(g0,g1)
    c: Coincident(g1,g2)
    c: Coincident(g2,g3)
    c: Coincident(g3,g0)
    c: Horizontal(g0)
    c: Horizontal(g2)
    c: Vertical(g1)
    c: Vertical(g3)
    c: Coincident(g0,g-5)
    c: PointOnObject(g1,g-4)
    c: DistanceY(g3,g3) = 5
FEATURE [PartDesign::Pad] Pad009
  BaseFeature = -> Pocket005
  Direction = (1,1,1)
  Length = 40
  Length2 = 100
  Placement = pos=(0,0,0) rot=(0.57735,0.57735,0.57735;2.0944rad)
  Profile = -> Sketch016
  Type = 0
FEATURE [Sketcher::SketchObject] Sketch017
  ExternalGeometry = -> [Pad009]
  FullyConstrained = true
  MapMode = 5
  Placement = pos=(0,-3.9e-15,-17.5482) rot=(0,0,-1;1.5708rad)
  Support = -> [Pad009]
  sketch-geometry (4):
    g0: LineSegment StartX=-27.4011 StartY=60 StartZ=0 EndX=27.0989 EndY=60 EndZ=0
    g1: LineSegment StartX=27.0989 StartY=60 StartZ=0 EndX=27.0989 EndY=56 EndZ=0
    g2: LineSegment StartX=27.0989 StartY=56 StartZ=0 EndX=-27.4011 EndY=56 EndZ=0
    g3: LineSegment StartX=-27.4011 StartY=56 StartZ=0 EndX=-27.4011 EndY=60 EndZ=0
  constraints (11):
    c: Coincident(g0,g1)
    c: Coincident(g1,g2)
    c: Coincident(g2,g3)
    c: Coincident(g3,g0)
    c: Horizontal(g0)
    c: Horizontal(g2)
    c: Vertical(g1)
    c: Vertical(g3)
    c: Coincident(g0,g-4)
    c: PointOnObject(g1,g-3)
    c: DistanceY(g1,g1) = 4
FEATURE [PartDesign::Pad] Pad010
  BaseFeature = -> Pad009
  Direction = (1,1,1)
  Length = 15
  Length2 = 100
  Placement = pos=(0,0,0) rot=(0.57735,0.57735,0.57735;2.0944rad)
  Profile = -> Sketch017
  Type = 0
FEATURE [PartDesign::Body] Body001
  Group = -> [Sketch004,Sketch002,Pad001,Pocket001,Sketch003,Pad006,Sketch013,Pad007,Sketch014,Pad008,Sketch015,Pocket005,Sketch016,Pad009,Sketch017,Pad010]
  Origin = -> Origin002
  Tip = -> Pad010
FEATURE [App::Part] Part001  label="ServoHolderPart"
  Group = -> [Body001]
  Origin = -> Origin003
---- part internalstructure.FCStd = doc fcstd_0d4ad100ca5e ----
FCSTD DOCUMENT  (FreeCAD 0.19R24366 (Git))
Label: internalstructure
License: All rights reserved
LicenseURL: http://en.wikipedia.org/wiki/All_rights_reserved
objects: Part::FeaturePython×46, App::FeaturePython×17, App::Link×11, Sketcher::SketchObject×9, PartDesign::Pad×5, PartDesign::Body×5, App::Part×5, PartDesign::Pocket×4
note: 77 computed .brp shape members not serialized (recipe doc carries the construction recipe); baked Part::Feature solids carry a one-line shape summary decoded from their .brp
EXTERNAL_REF file=MotorAndHolder_v1.FCStd obj=Part001
EXTERNAL_REF file=Battery_VoltaicV70.FCStd obj=Part
EXTERNAL_REF file=MotorAndHolder_v1.FCStd obj=Part006
EXTERNAL_REF file=test.FCStd obj=Part

FEATURE [Sketcher::SketchObject] Sketch  label="ServoHolder"
  FullyConstrained = false
  MapMode = 4
  Placement = pos=(0,0,0) rot=(0.57735,0.57735,0.57735;2.0944rad)
  sketch-geometry (8):
    g0: LineSegment StartX=-27.0989 StartY=-22.5482 StartZ=0 EndX=27.4011 EndY=-22.5482 EndZ=0
    g1: LineSegment StartX=20.6511 StartY=-19.5482 StartZ=0 EndX=20.6511 EndY=8.45178 EndZ=0
    g2: LineSegment StartX=20.6511 StartY=8.45178 StartZ=0 EndX=27.4011 EndY=8.45178 EndZ=0
    g3: LineSegment StartX=-20.3489 StartY=-19.5482 StartZ=0 EndX=-20.3489 EndY=8.45178 EndZ=0
    g4: LineSegment StartX=-20.3489 StartY=8.45178 StartZ=0 EndX=-27.0989 EndY=8.45178 EndZ=0
    g5: LineSegment StartX=20.6511 StartY=-19.5482 StartZ=0 EndX=-20.3489 EndY=-19.5482 EndZ=0
    g6: LineSegment StartX=-27.0989 StartY=8.45178 StartZ=0 EndX=-27.0989 EndY=-22.5482 EndZ=0
    g7: LineSegment StartX=27.4011 StartY=8.45178 StartZ=0 EndX=27.4011 EndY=-22.5482 EndZ=0
  constraints (22):
    c: Horizontal(g0)
    c: Coincident(g1,g2)
    c: Horizontal(g2)
    c: Vertical(g1)
    c: Coincident(g3,g4)
    c: Horizontal(g4)
    c: Vertical(g3)
    c: Coincident(g5,g1)
    c: Coincident(g5,g3)
    c: Horizontal(g5)
    c: Coincident(g6,g4)
    c: Coincident(g6,g0)
    c: Vertical(g6)
    c: Coincident(g7,g2)
    c: Coincident(g7,g0)
    c: Vertical(g7)
    c: DistanceX(g0,g0) = 54.5
    c: DistanceX(g5,g5) = 41
    c: Equal(g4,g2)
    c: Horizontal(g3,g1)
    c: DistanceY(g0,g1) = 3
    c: DistanceY(g1,g1) = 28
FEATURE [PartDesign::Pad] Pad  label="ExtrudeServoHolder"
  Direction = (1,1,1)
  Length = 20
  Length2 = 100
  Placement = pos=(0,0,0) rot=(0.57735,0.57735,0.57735;2.0944rad)
  Profile = -> Sketch
  Type = 0
FEATURE [Sketcher::SketchObject] Sketch001  label="WireHoleSketch"
  FullyConstrained = false
  Placement = pos=(0,27.4011,0) rot=(0,0.707107,0.707107;3.14159rad)
  sketch-geometry (4):
    g0: LineSegment StartX=-5.36505 StartY=-10.7623 StartZ=0 EndX=-14.3651 EndY=-10.7623 EndZ=0
    g1: LineSegment StartX=-14.3651 StartY=-10.7623 StartZ=0 EndX=-14.3651 EndY=-16.7623 EndZ=0
    g2: LineSegment StartX=-14.3651 StartY=-16.7623 StartZ=0 EndX=-5.36505 EndY=-16.7623 EndZ=0
    g3: LineSegment StartX=-5.36505 StartY=-16.7623 StartZ=0 EndX=-5.36505 EndY=-10.7623 EndZ=0
  constraints (10):
    c: Coincident(g1,g2)
    c: Coincident(g2,g3)
    c: Coincident(g3,g0)
    c: Horizontal(g0)
    c: Horizontal(g2)
    c: Vertical(g1)
    c: Vertical(g3)
    c: Coincident(g1,g0)
    c: DistanceX(g0,g0) = 9
    c: DistanceY(g1,g1) = 6
FEATURE [PartDesign::Pocket] Pocket  label="ServoHolder001"
  BaseFeature = -> Pad
  Length = 8
  Length2 = 100
  Placement = pos=(0,0,0) rot=(0.57735,0.57735,0.57735;2.0944rad)
  Profile = -> Sketch001
  Type = 0
FEATURE [Sketcher::SketchObject] Sketch002  label="HorizontalSupportHole"
  FullyConstrained = false
  MapMode = 5
  Placement = pos=(0,0,0) rot=(0.57735,0.57735,-0.57735;4.18879rad)
  Support = -> [Pocket]
  sketch-geometry (8):
    g0: LineSegment StartX=-25.8969 StartY=20.9931 StartZ=0 EndX=-21.6969 EndY=20.9931 EndZ=0
    g1: LineSegment StartX=-21.6969 StartY=20.9931 StartZ=0 EndX=-21.6969 EndY=16.7931 EndZ=0
    g2: LineSegment StartX=-21.6969 StartY=16.7931 StartZ=0 EndX=-25.8969 EndY=16.7931 EndZ=0
    g3: LineSegment StartX=-25.8969 StartY=16.7931 StartZ=0 EndX=-25.8969 EndY=20.9931 EndZ=0
    g4: LineSegment StartX=26.0415 StartY=16.7931 StartZ=0 EndX=21.8415 EndY=16.7931 EndZ=0
    g5: LineSegment StartX=21.8415 StartY=16.7931 StartZ=0 EndX=21.8415 EndY=20.9931 EndZ=0
    g6: LineSegment StartX=21.8415 StartY=20.9931 StartZ=0 EndX=26.0415 EndY=20.9931 EndZ=0
    g7: LineSegment StartX=26.0415 StartY=20.9931 StartZ=0 EndX=26.0415 EndY=16.7931 EndZ=0
  constraints (21):
    c: Coincident(g0,g1)
    c: Coincident(g1,g2)
    c: Coincident(g2,g3)
    c: Coincident(g3,g0)
    c: Horizontal(g0)
    c: Horizontal(g2)
    c: Vertical(g1)
    c: Vertical(g3)
    c: Equal(g0,g1)
    c: DistanceY(g1,g1) = 4.2
    c: Coincident(g4,g5)
    c: Coincident(g5,g6)
    c: Coincident(g6,g7)
    c: Coincident(g7,g4)
    c: Horizontal(g4)
    c: Horizontal(g6)
    c: Vertical(g5)
    c: Vertical(g7)
    c: Equal(g4,g5)
    c: DistanceY(g5,g5) = 4.2  'support_width'
    c: Horizontal(g4,g1)
FEATURE [PartDesign::Pocket] Pocket001  label="SupportPocket"
  BaseFeature = -> Pocket
  Length = 5
  Length2 = 100
  Placement = pos=(0,0,0) rot=(0.57735,0.57735,0.57735;2.0944rad)
  Profile = -> Sketch002
  Type = 0
FEATURE [PartDesign::Body] Body
  Group = -> [Sketch001,Sketch,Pad,Pocket,Sketch002,Pocket001]
  Origin = -> Origin001
  Tip = -> Pocket001
FEATURE [App::Part] Part  label="ServoHolderPart"
  Group = -> [Body]
  Origin = -> Origin
FEATURE [Sketcher::SketchObject] Sketch003  label="HorizontalSupport001"
  FullyConstrained = false
  Placement = pos=(3e-15,0,0) rot=(0.57735,0.57735,-0.57735;4.18879rad)
  sketch-geometry (4):
    g0: LineSegment StartX=-25.8969 StartY=20.9914 StartZ=0 EndX=-21.8969 EndY=20.9914 EndZ=0
    g1: LineSegment StartX=-21.8969 StartY=20.9914 StartZ=0 EndX=-21.8969 EndY=16.9914 EndZ=0
    g2: LineSegment StartX=-21.8969 StartY=16.9914 StartZ=0 EndX=-25.8969 EndY=16.9914 EndZ=0
    g3: LineSegment StartX=-25.8969 StartY=16.9914 StartZ=0 EndX=-25.8969 EndY=20.9914 EndZ=0
  constraints (10):
    c: Coincident(g0,g1)
    c: Coincident(g1,g2)
    c: Coincident(g2,g3)
    c: Coincident(g3,g0)
    c: Horizontal(g0)
    c: Horizontal(g2)
    c: Vertical(g1)
    c: Vertical(g3)
    c: Equal(g0,g1)
    c: DistanceY(g1,g1) = 4
FEATURE [PartDesign::Pad] Pad001
  Direction = (1,1,1)
  Length = 150
  Length2 = 100
  Placement = pos=(3e-15,0,0) rot=(0.57735,0.57735,-0.57735;4.18879rad)
  Profile = -> Sketch003
  Type = 0
FEATURE [PartDesign::Body] Body001
  Group = -> [Sketch003,Pad001]
  Origin = -> Origin003
  Tip = -> Pad001
FEATURE [App::Part] Part001  label="Connector4x4x120mm"
  Group = -> [Body001]
  Origin = -> Origin002
FEATURE [Sketcher::SketchObject] Sketch008
  FullyConstrained = false
  Placement = pos=(-120,-7e-15,-22.4909) rot=(0.707107,-0.707107,0;3.14159rad)
  sketch-geometry (6):
    g0: LineSegment StartX=17.1768 StartY=6.75 StartZ=0 EndX=20.6768 EndY=6.75 EndZ=0
    g1: LineSegment StartX=20.6768 StartY=6.75 StartZ=0 EndX=20.6768 EndY=3.25 EndZ=0
    g2: LineSegment StartX=20.6768 StartY=3.25 StartZ=0 EndX=17.1768 EndY=3.25 EndZ=0
    g3: LineSegment StartX=17.1768 StartY=3.25 StartZ=0 EndX=17.1768 EndY=6.75 EndZ=0
    g4: LineSegment StartX=17.1768 StartY=3.25 StartZ=0 EndX=17.1768 EndY=0 EndZ=0
    g5: LineSegment StartX=17.1768 StartY=6.75 StartZ=0 EndX=17.1768 EndY=10 EndZ=0
  constraints (16):
    c: Coincident(g0,g1)
    c: Coincident(g1,g2)
    c: Coincident(g2,g3)
    c: Coincident(g3,g0)
    c: Horizontal(g0)
    c: Horizontal(g2)
    c: Vertical(g1)
    c: Vertical(g3)
    c: Equal(g0,g1)
    c: DistanceX(g0,g0) = 3.5
    c: Coincident(g4,g2)
    c: PointOnObject(g4,g-1)
    c: Vertical(g4)
    c: Coincident(g5,g0)
    c: Vertical(g5)
    c: Equal(g5,g4)
FEATURE [PartDesign::Pad] Pad003
  Direction = (1,1,1)
  Length = 72
  Length2 = 100
  Placement = pos=(-120,-7e-15,-22.4909) rot=(0.707107,-0.707107,0;3.14159rad)
  Profile = -> Sketch008
  Type = 0
FEATURE [PartDesign::Body] Body003
  Group = -> [Sketch008,Pad003]
  Origin = -> Origin006
  Tip = -> Pad003
FEATURE [App::Part] Part003  label="Connector4x4x72mm"
  Group = -> [Body003]
  Origin = -> Origin007
FEATURE [Sketcher::SketchObject] Sketch009
  FullyConstrained = false
  Placement = pos=(-120,3.5e-14,-72.4909) rot=(0.707107,-0.707107,0;3.14159rad)
  sketch-geometry (4):
    g0: LineSegment StartX=-22.0524 StartY=7.96105 StartZ=0 EndX=21.7963 EndY=7.96105 EndZ=0
    g1: LineSegment StartX=21.7963 StartY=7.96105 StartZ=0 EndX=21.7963 EndY=2.30544 EndZ=0
    g2: LineSegment StartX=21.7963 StartY=2.30544 StartZ=0 EndX=-22.0524 EndY=2.30544 EndZ=0
    g3: LineSegment StartX=-22.0524 StartY=2.30544 StartZ=0 EndX=-22.0524 EndY=7.96105 EndZ=0
  constraints (8):
    c: Coincident(g0,g1)
    c: Coincident(g1,g2)
    c: Coincident(g2,g3)
    c: Coincident(g3,g0)
    c: Horizontal(g0)
    c: Horizontal(g2)
    c: Vertical(g1)
    c: Vertical(g3)
FEATURE [Sketcher::SketchObject] Sketch010
  FullyConstrained = false
  Placement = pos=(-120,2.3e-14,-72.4909) rot=(0,0,-1;1.5708rad)
  sketch-geometry (8):
    g0: LineSegment StartX=16.8176 StartY=-7.09377 StartZ=0 EndX=21.0176 EndY=-7.09377 EndZ=0
    g1: LineSegment StartX=21.0176 StartY=-7.09377 StartZ=0 EndX=21.0176 EndY=-2.89377 EndZ=0
    g2: LineSegment StartX=21.0176 StartY=-2.89377 StartZ=0 EndX=16.8176 EndY=-2.89377 EndZ=0
    g3: LineSegment StartX=16.8176 StartY=-2.89377 StartZ=0 EndX=16.8176 EndY=-7.09377 EndZ=0
    g4: LineSegment StartX=-17.1303 StartY=-7.13419 StartZ=0 EndX=-21.3303 EndY=-7.13419 EndZ=0
    g5: LineSegment StartX=-21.3303 StartY=-7.13419 StartZ=0 EndX=-21.3303 EndY=-2.93419 EndZ=0
    g6: LineSegment StartX=-21.3303 StartY=-2.93419 StartZ=0 EndX=-17.1303 EndY=-2.93419 EndZ=0
    g7: LineSegment StartX=-17.1303 StartY=-2.93419 StartZ=0 EndX=-17.1303 EndY=-7.13419 EndZ=0
  constraints (20):
    c: Coincident(g0,g1)
    c: Coincident(g1,g2)
    c: Coincident(g2,g3)
    c: Coincident(g3,g0)
    c: Horizontal(g0)
    c: Horizontal(g2)
    c: Vertical(g1)
    c: Vertical(g3)
    c: Equal(g2,g1)
    c: DistanceX(g2,g2) = 4.2
    c: Coincident(g4,g5)
    c: Coincident(g5,g6)
    c: Coincident(g6,g7)
    c: Coincident(g7,g4)
    c: Horizontal(g4)
    c: Horizontal(g6)
    c: Vertical(g5)
    c: Vertical(g7)
    c: Equal(g5,g6)
    c: DistanceX(g6,g6) = 4.2
FEATURE [PartDesign::Pad] Pad004
  Direction = (1,1,1)
  Length = 4
  Length2 = 100
  Placement = pos=(-120,3.5e-14,-72.4909) rot=(0.707107,-0.707107,0;3.14159rad)
  Profile = -> Sketch009
  Type = 0
FEATURE [PartDesign::Pocket] Pocket004
  BaseFeature = -> Pad004
  Length = 3
  Length2 = 100
  Placement = pos=(-120,3.5e-14,-72.4909) rot=(0.707107,-0.707107,0;3.14159rad)
  Profile = -> Sketch010
  Type = 0
FEATURE [PartDesign::Body] Body004
  Group = -> [Sketch009,Sketch010,Pad004,Pocket004]
  Origin = -> Origin009
  Tip = -> Pocket004
FEATURE [App::Part] Part004  label="BatteryBottomConnector"
  Group = -> [Body004]
  Origin = -> Origin008
FEATURE [App::Link] Link010  label="StarboardConnector4x4x120mm001"
  LinkPlacement = pos=(-77,65,-6) rot=(0,0,1;0rad)
  LinkedObject = -> Part001
  Placement = pos=(-77,65,-6) rot=(0,0,1;0rad)
FEATURE [App::Link] Link009  label="PortConnector4x4x120mm"
  LinkPlacement = pos=(-77,17.3124,-6) rot=(0,0,1;0rad)
  LinkedObject = -> Part001
  Placement = pos=(-77,17.3124,-6) rot=(0,0,1;0rad)
FEATURE [App::Link] Link008  label="ServoHolderPart001"
  LinkPlacement = pos=(-82,17.1616,-6.09826) rot=(0,0,1;0rad)
  LinkedObject = -> Part
  Placement = pos=(-82,17.1616,-6.09826) rot=(0,0,1;0rad)
FEATURE [App::Link] Link013  label="Connector4x4x50mm_1"
  LinkPlacement = pos=(-58.3113,-32.47,-6.94535) rot=(0.406768,0.422033,-0.810202;1.09346rad)
  LinkedObject = -> Part003
  Placement = pos=(-58.3113,-32.47,-6.94535) rot=(0.406768,0.422033,-0.810202;1.09346rad)
FEATURE [App::Link] Link014  label="Connector4x4x50mm_002"
  LinkPlacement = pos=(-27.2761,-11.2422,-0.204668) rot=(0.406768,0.422033,-0.810202;1.09346rad)
  LinkedObject = -> Part003
  Placement = pos=(-27.2761,-11.2422,-0.204668) rot=(0.406768,0.422033,-0.810202;1.09346rad)
FEATURE [App::Link] Link015  label="BatteryBottomConnector001"
  LinkPlacement = pos=(-61.995,-22.0909,-22.4278) rot=(0.406768,0.422033,-0.810202;1.09346rad)
  LinkedObject = -> Part004
  Placement = pos=(-61.995,-22.0909,-22.4278) rot=(0.406768,0.422033,-0.810202;1.09346rad)
FEATURE [App::Link] Link  label="MotorHolder"
  LinkPlacement = pos=(-150.627,76.7929,74.012) rot=(0.941206,0.243222,0.234468;2.26967rad)
  LinkedObject = -> <external MotorAndHolder_v1.FCStd>#Part001
  Placement = pos=(-150.627,76.7929,74.012) rot=(0.941206,0.243222,0.234468;2.26967rad)
FEATURE [App::Link] Link016  label="PartBatteryVoltaicV70"
  LinkPlacement = pos=(-373,0.000171781,-93) rot=(0.548548,0.681735,0.484079;4.28615rad)
  LinkedObject = -> <external Battery_VoltaicV70.FCStd>#Part
  Placement = pos=(-373,0.000171781,-93) rot=(0.548548,0.681735,0.484079;4.28615rad)
FEATURE [App::Link] Link017  label="ConnectorRod2.5x200mm001"
  LinkPlacement = pos=(-93.8892,30.3514,15.7073) rot=(-0.529261,-0.748426,-0.399677;1.08373rad)
  LinkedObject = -> <external MotorAndHolder_v1.FCStd>#Part006
  Placement = pos=(-93.8892,30.3514,15.7073) rot=(-0.529261,-0.748426,-0.399677;1.08373rad)
FEATURE [App::Link] Link018  label="ConnectorRod2.5x200mm002"
  LinkPlacement = pos=(-114.238,23.92,16.3093) rot=(-0.736688,-0.674933,-0.041909;0.985761rad)
  LinkedObject = -> <external MotorAndHolder_v1.FCStd>#Part006
  Placement = pos=(-114.238,23.92,16.3093) rot=(-0.736688,-0.674933,-0.041909;0.985761rad)
FEATURE [Sketcher::SketchObject] Sketch004
  FullyConstrained = false
  Placement = pos=(-120,-2.7e-14,-4e-14) rot=(0.57735,0.57735,-0.57735;4.18879rad)
  sketch-geometry (4):
    g0: LineSegment StartX=-26.9181 StartY=22.4909 StartZ=0 EndX=27.2601 EndY=22.4909 EndZ=0
    g1: LineSegment StartX=27.2601 StartY=22.4909 StartZ=0 EndX=27.2601 EndY=15.6382 EndZ=0
    g2: LineSegment StartX=27.2601 StartY=15.6382 StartZ=0 EndX=-26.9181 EndY=15.6382 EndZ=0
    g3: LineSegment StartX=-26.9181 StartY=15.6382 StartZ=0 EndX=-26.9181 EndY=22.4909 EndZ=0
  constraints (8):
    c: Coincident(g0,g1)
    c: Coincident(g1,g2)
    c: Coincident(g2,g3)
    c: Coincident(g3,g0)
    c: Horizontal(g0)
    c: Horizontal(g2)
    c: Vertical(g1)
    c: Vertical(g3)
FEATURE [PartDesign::Pad] Pad002
  Direction = (1,1,1)
  Length = 10
  Length2 = 100
  Placement = pos=(-120,-2.7e-14,-4e-14) rot=(0.57735,0.57735,-0.57735;4.18879rad)
  Profile = -> Sketch004
  Type = 0
FEATURE [Sketcher::SketchObject] Sketch011
  ExternalGeometry = -> [Pad002]
  FullyConstrained = false
  MapMode = 5
  Placement = pos=(-130,-2.7e-14,-4e-14) rot=(0.57735,0.57735,-0.57735;4.18879rad)
  Support = -> [Pad002]
  sketch-geometry (6):
    g0: Circle CenterX=-10 CenterY=18.8622 CenterZ=0 NormalX=0 NormalY=0 NormalZ=1 AngleXU=0 Radius=1.4
    g1: Circle CenterX=10 CenterY=18.8622 CenterZ=0 NormalX=0 NormalY=0 NormalZ=1 AngleXU=0 Radius=1.4
    g2: LineSegment StartX=10 StartY=18.8622 StartZ=0 EndX=0 EndY=18.8622 EndZ=0
    g3: LineSegment StartX=-10 StartY=18.8622 StartZ=0 EndX=0 EndY=18.8622 EndZ=0
    g4: LineSegment StartX=-26.9181 StartY=18.8622 StartZ=0 EndX=-10 EndY=18.8622 EndZ=0
    g5: LineSegment StartX=10 StartY=18.8622 StartZ=0 EndX=27.2601 EndY=18.8622 EndZ=0
  constraints (16):
    c: Horizontal(g1,g0)
    c: Coincident(g2,g1)
    c: PointOnObject(g2,g-2)
    c: Horizontal(g2)
    c: Coincident(g3,g0)
    c: Coincident(g3,g2)
    c: Equal(g2,g3)
    c: DistanceX(g0,g1) = 20
    c: Equal(g0,g1)
    c: Diameter(g0) = 2.8
    c: PointOnObject(g4,g-4)
    c: Horizontal(g4)
    c: Coincident(g5,g1)
    c: PointOnObject(g5,g-3)
    c: Horizontal(g5)
    c: Coincident(g0,g4)
FEATURE [PartDesign::Pocket] Pocket005
  BaseFeature = -> Pad002
  Length = 25
  Length2 = 100
  Placement = pos=(-120,-2.7e-14,-4e-14) rot=(0.57735,0.57735,-0.57735;4.18879rad)
  Profile = -> Sketch011
  Type = 0
FEATURE [PartDesign::Body] Body002
  Group = -> [Sketch004,Pad002,Sketch011,Pocket005]
  Origin = -> Origin005
  Tip = -> Pocket005
FEATURE [App::Part] Part002  label="BatteryVerticalConnect"
  Group = -> [Body002]
  Origin = -> Origin004
  Placement = pos=(-61.525,-15.3822,-45.9494) rot=(0.873997,-0.430968,-0.22449;3.56776rad)
FEATURE [App::Link] Link019  label="Connector"
  LinkPlacement = pos=(-178.657,-39.8223,-130.615) rot=(-0.086869,0.081007,0.992921;1.64769rad)
  LinkedObject = -> <external test.FCStd>#Part
  Placement = pos=(-178.657,-39.8223,-130.615) rot=(-0.086869,0.081007,0.992921;1.64769rad)
FEATURE [Part::FeaturePython] Parts001  # WARN: FeaturePython — macro-defined, semantics opaque (R4)
  Group = -> [Link008,Link009,Link010,Link014,Link013,Link015,Link,Link017,Link018,Part002,Link019]
  GroupMode = 0
FEATURE [Part::FeaturePython] _Element024  # link proxy (typed FeaturePython)
  Detach = false
  LinkTransform = true
  LinkedObject = -> Link010 [Body001.Pad001.Face4]
  _Parent = -> Elements001
FEATURE [Part::FeaturePython] _Element028  # link proxy (typed FeaturePython)
  Detach = false
  LinkTransform = true
  LinkedObject = -> Link009 [Body001.Pad001.Face2]
  _Parent = -> Elements001
FEATURE [Part::FeaturePython] _Element030  # link proxy (typed FeaturePython)
  Detach = false
  LinkTransform = true
  LinkedObject = -> Link010 [Body001.Pad001.Face6]
  _Parent = -> Elements001
FEATURE [Part::FeaturePython] _Element031  # link proxy (typed FeaturePython)
  Detach = false
  LinkTransform = true
  LinkedObject = -> Link009 [Body001.Pad001.Face6]
  _Parent = -> Elements001
FEATURE [Part::FeaturePython] _Element032  # link proxy (typed FeaturePython)
  Detach = false
  LinkTransform = true
  LinkedObject = -> Link008 [Body.Pocket001.Face23]
  _Parent = -> Elements001
FEATURE [Part::FeaturePython] _Element033  # link proxy (typed FeaturePython)
  Detach = false
  LinkTransform = true
  LinkedObject = -> Link010 [Body001.Pad001.Face5]
  _Parent = -> Elements001
FEATURE [Part::FeaturePython] _Element034  # link proxy (typed FeaturePython)
  Detach = false
  LinkTransform = true
  LinkedObject = -> Link008 [Body.Pocket001.Face22]
  _Parent = -> Elements001
FEATURE [App::FeaturePython] ElementLink014  label="_Element034"  # link proxy (typed FeaturePython)
  LinkTransform = true
  LinkedObject = -> _Element034
  _Parent = -> Constraint007
FEATURE [Part::FeaturePython] _Element035  # link proxy (typed FeaturePython)
  Detach = false
  LinkTransform = true
  LinkedObject = -> Link009 [Body001.Pad001.Face4]
  _Parent = -> Elements001
FEATURE [App::FeaturePython] ElementLink015  label="_Element035"  # link proxy (typed FeaturePython)
  LinkTransform = true
  LinkedObject = -> _Element035
  _Parent = -> Constraint007
FEATURE [App::FeaturePython] Constraint007  label="SameOrientation001"  # WARN: FeaturePython — macro-defined, semantics opaque (R4)
  Disabled = false
  Group = -> [ElementLink014,ElementLink015]
  _ConstraintType = 2
  _Parent = -> Constraints001
FEATURE [Part::FeaturePython] _Element044  # link proxy (typed FeaturePython)
  Detach = false
  LinkTransform = true
  LinkedObject = -> Link013 [Body003.Pad003.Face2]
  _Parent = -> Elements001
FEATURE [Part::FeaturePython] _Element037  # link proxy (typed FeaturePython)
  Detach = false
  LinkTransform = true
  LinkedObject = -> Link013 [Body003.Pad003.Face5]
  _Parent = -> Elements001
FEATURE [Part::FeaturePython] _Element046  # link proxy (typed FeaturePython)
  Detach = false
  LinkTransform = true
  LinkedObject = -> Link014 [Body003.Pad003.Face5]
  _Parent = -> Elements001
FEATURE [Part::FeaturePython] _Element047  # link proxy (typed FeaturePython)
  Detach = false
  LinkTransform = true
  LinkedObject = -> Link014 [Body003.Pad003.Face1]
  _Parent = -> Elements001
FEATURE [Part::FeaturePython] _Element026  # link proxy (typed FeaturePython)
  Detach = false
  LinkTransform = true
  LinkedObject = -> Link010 [Body001.Pad001.Face3]
  _Parent = -> Elements001
FEATURE [Part::FeaturePython] _Element053  # link proxy (typed FeaturePython)
  Detach = false
  LinkTransform = true
  LinkedObject = -> Link009 [Body001.Pad001.Face3]
  _Parent = -> Elements001
FEATURE [Part::FeaturePython] _Element054  # link proxy (typed FeaturePython)
  Detach = false
  LinkTransform = true
  LinkedObject = -> Link015 [Body004.Pocket004.Face16]
  _Parent = -> Elements001
FEATURE [App::FeaturePython] ElementLink032  label="_Element054"  # link proxy (typed FeaturePython)
  LinkTransform = true
  LinkedObject = -> _Element054
  _Parent = -> Constraint016
FEATURE [Part::FeaturePython] _Element055  # link proxy (typed FeaturePython)
  Detach = false
  LinkTransform = true
  LinkedObject = -> Link014 [Body003.Pad003.Face6]
  _Parent = -> Elements001
FEATURE [App::FeaturePython] ElementLink033  label="_Element055"  # link proxy (typed FeaturePython)
  LinkTransform = true
  LinkedObject = -> _Element055
  _Parent = -> Constraint016
FEATURE [App::FeaturePython] Constraint016  label="PlaneCoincident004"  # WARN: FeaturePython — macro-defined, semantics opaque (R4)
  Angle = 0
  AnglePitch = 0
  AngleRoll = 0
  Cascade = false
  Disabled = false
  Group = -> [ElementLink032,ElementLink033]
  LockAngle = false
  Multiply = false
  OffsetX = 0
  OffsetY = 0
  _ConstraintType = 35
  _Parent = -> Constraints001
FEATURE [Part::FeaturePython] _Element056  # link proxy (typed FeaturePython)
  Detach = false
  LinkTransform = true
  LinkedObject = -> Link014 [Body003.Pad003.Face4]
  _Parent = -> Elements001
FEATURE [App::FeaturePython] ElementLink034  label="_Element056"  # link proxy (typed FeaturePython)
  LinkTransform = true
  LinkedObject = -> _Element056
  _Parent = -> Constraint017
FEATURE [Part::FeaturePython] _Element057  # link proxy (typed FeaturePython)
  Detach = false
  LinkTransform = true
  LinkedObject = -> Link015 [Body004.Pocket004.Face13]
  _Parent = -> Elements001
FEATURE [App::FeaturePython] ElementLink035  label="_Element057"  # link proxy (typed FeaturePython)
  LinkTransform = true
  LinkedObject = -> _Element057
  _Parent = -> Constraint017
FEATURE [App::FeaturePython] Constraint017  label="MultiParallel001"  # WARN: FeaturePython — macro-defined, semantics opaque (R4)
  Angle = 0
  AnglePitch = 0
  AngleRoll = 0
  Disabled = false
  Group = -> [ElementLink034,ElementLink035]
  LockAngle = false
  _ConstraintType = 291
  _Parent = -> Constraints001
FEATURE [App::FeaturePython] Constraints001  # WARN: FeaturePython — macro-defined, semantics opaque (R4)
  Group = -> [Constraint007,Constraint016,Constraint017,Constraint018,Constraint020]
  _Version = 1
FEATURE [Part::FeaturePython] _Element039  # link proxy (typed FeaturePython)
  Detach = false
  LinkTransform = true
  LinkedObject = -> Link013 [Body003.Pad003.Face1]
  _Parent = -> Elements001
FEATURE [Part::FeaturePython] _Element041  # link proxy (typed FeaturePython)
  Detach = false
  LinkTransform = true
  LinkedObject = -> Link013 [Body003.Pad003.Face4]
  _Parent = -> Elements001
FEATURE [Part::FeaturePython] _Element050  # link proxy (typed FeaturePython)
  Detach = false
  LinkTransform = true
  LinkedObject = -> Link010 [Body001.Pad001.Face1]
  _Parent = -> Elements001
FEATURE [App::FeaturePython] Elements001  # WARN: FeaturePython — macro-defined, semantics opaque (R4)
  Group = -> [_Element024,_Element026,_Element028,_Element030,_Element031,_Element032,_Element033,_Element034,_Element035,_Element037,_Element039,_Element041,_Element044,_Element046,_Element047,_Element050,_Element053,_Element054,_Element055,_Element056,_Element057,Element,Element001,Element002,Element003,Element004,_Element,_Element061,_Element062,_Element064,_Element065,Element005,Element006,Element007,+10 more]
FEATURE [Part::FeaturePython] Assembly001  label="InternalHolder"  # WARN: FeaturePython — macro-defined, semantics opaque (R4)
  AutoRelax = true
  BuildShape = 0
  Freeze = false
  Group = -> [Constraints001,Elements001,Parts001]
  Verbose = false
  _SolverType = 1
  _Version = 1
FEATURE [Part::FeaturePython] Element  # link proxy (typed FeaturePython)
  Detach = false
  LinkTransform = true
  LinkedObject = -> Link015 [Body004.Pocket004.Face4]
  _Parent = -> Elements001
FEATURE [Part::FeaturePython] Element001  # link proxy (typed FeaturePython)
  Detach = false
  LinkTransform = true
  LinkedObject = -> Link014 [Body003.Pad003.Face2]
  _Parent = -> Elements001
FEATURE [Part::FeaturePython] Element002  # link proxy (typed FeaturePython)
  Detach = false
  LinkTransform = true
  LinkedObject = -> Link008 [Body.Pocket001.Face1]
  _Parent = -> Elements001
FEATURE [Part::FeaturePython] Element003  # link proxy (typed FeaturePython)
  Detach = false
  LinkTransform = true
  LinkedObject = -> Link008 [Body.Pocket001.Face2]
  _Parent = -> Elements001
FEATURE [Part::FeaturePython] Element004  # link proxy (typed FeaturePython)
  Detach = false
  LinkTransform = true
  LinkedObject = -> Link008 [Body.Pocket001.Face11]
  _Parent = -> Elements001
FEATURE [Part::FeaturePython] _Element  # link proxy (typed FeaturePython)
  Detach = false
  LinkTransform = true
  LinkedObject = -> Link [Body001.Pocket003.Face17]
  _Parent = -> Elements001
FEATURE [Part::FeaturePython] _Element061  # link proxy (typed FeaturePython)
  Detach = false
  LinkTransform = true
  LinkedObject = -> Link017 [Body006.Pad006.Face1]
  _Parent = -> Elements001
FEATURE [App::FeaturePython] Constraint018  label="AxialAlignment001"  # WARN: FeaturePython — macro-defined, semantics opaque (R4)
  Angle = 0
  AnglePitch = 0
  AngleRoll = 0
  Disabled = false
  Group = -> [ElementLink037,ElementLink038]
  LockAngle = false
  Multiply = false
  _ConstraintType = 36
  _Parent = -> Constraints001
FEATURE [App::FeaturePython] ElementLink037  label="_Element062"  # link proxy (typed FeaturePython)
  LinkTransform = true
  LinkedObject = -> _Element062
  _Parent = -> Constraint018
FEATURE [Part::FeaturePython] _Element062  # link proxy (typed FeaturePython)
  Detach = false
  LinkTransform = true
  LinkedObject = -> Link [Body001.Pocket004.Face17]
  _Parent = -> Elements001
FEATURE [App::FeaturePython] ElementLink038  label="_Element061"  # link proxy (typed FeaturePython)
  LinkTransform = true
  LinkedObject = -> _Element061
  _Parent = -> Constraint018
FEATURE [Part::FeaturePython] _Element064  # link proxy (typed FeaturePython)
  Detach = false
  LinkTransform = true
  LinkedObject = -> Link018 [Body006.Pad006.Face1]
  _Parent = -> Elements001
FEATURE [App::FeaturePython] Constraint020  label="AxialAlignment003"  # WARN: FeaturePython — macro-defined, semantics opaque (R4)
  Angle = 0
  AnglePitch = 0
  AngleRoll = 0
  Disabled = false
  Group = -> [ElementLink041,ElementLink042]
  LockAngle = false
  Multiply = false
  _ConstraintType = 36
  _Parent = -> Constraints001
FEATURE [App::FeaturePython] ElementLink041  label="_Element064"  # link proxy (typed FeaturePython)
  LinkTransform = true
  LinkedObject = -> _Element064
  _Parent = -> Constraint020
FEATURE [App::FeaturePython] ElementLink042  label="_Element065"  # link proxy (typed FeaturePython)
  LinkTransform = true
  LinkedObject = -> _Element065
  _Parent = -> Constraint020
FEATURE [Part::FeaturePython] _Element065  # link proxy (typed FeaturePython)
  Detach = false
  LinkTransform = true
  LinkedObject = -> Link [Body001.Pocket004.Face18]
  _Parent = -> Elements001
FEATURE [Part::FeaturePython] Element005  # link proxy (typed FeaturePython)
  Detach = false
  LinkTransform = true
  LinkedObject = -> Link [Body001.Pocket004.Face7]
  _Parent = -> Elements001
FEATURE [Part::FeaturePython] Element006  # link proxy (typed FeaturePython)
  Detach = false
  LinkTransform = true
  LinkedObject = -> Link [Body001.Pocket004.Face4]
  _Parent = -> Elements001
FEATURE [Part::FeaturePython] Element007  # link proxy (typed FeaturePython)
  Detach = false
  LinkTransform = true
  LinkedObject = -> Link [Body001.Pocket004.Face3]
  _Parent = -> Elements001
FEATURE [Part::FeaturePython] Element008  # link proxy (typed FeaturePython)
  Detach = false
  LinkTransform = true
  LinkedObject = -> Link [Body001.Pocket004.Face14]
  _Parent = -> Elements001
FEATURE [Part::FeaturePython] Element009  # link proxy (typed FeaturePython)
  Detach = false
  LinkTransform = true
  LinkedObject = -> Link [Body001.Pocket004.Face13]
  _Parent = -> Elements001
FEATURE [Part::FeaturePython] Element010  # link proxy (typed FeaturePython)
  Detach = false
  LinkTransform = true
  LinkedObject = -> Link [Body001.Pocket004.Edge11]
  _Parent = -> Elements001
FEATURE [Part::FeaturePython] Element011  # link proxy (typed FeaturePython)
  Detach = false
  LinkTransform = true
  LinkedObject = -> Link [Body001.Pocket004.Face5]
  _Parent = -> Elements001
FEATURE [Part::FeaturePython] Element012  # link proxy (typed FeaturePython)
  Detach = false
  LinkTransform = true
  LinkedObject = -> Link017 [Body006.Pad006.Edge1]
  _Parent = -> Elements001
FEATURE [Part::FeaturePython] Element014  # link proxy (typed FeaturePython)
  Detach = false
  LinkTransform = true
  LinkedObject = -> Link [Body001.Pocket004.Face20]
  _Parent = -> Elements001
FEATURE [Part::FeaturePython] Element015  # link proxy (typed FeaturePython)
  Detach = false
  LinkTransform = true
  LinkedObject = -> Link015 [Body004.Pocket004.Face2]
  _Parent = -> Elements001
FEATURE [Part::FeaturePython] Element018  # link proxy (typed FeaturePython)
  Detach = false
  LinkTransform = true
  LinkedObject = -> Link015 [Body004.Pocket004.Face6]
  _Parent = -> Elements001
FEATURE [Part::FeaturePython] _Element066  # link proxy (typed FeaturePython)
  Detach = false
  LinkTransform = true
  LinkedObject = -> Link019 [Body.Pad.Face10]
  _Parent = -> Elements001
FEATURE [Part::FeaturePython] _Element067  # link proxy (typed FeaturePython)
  Detach = false
  LinkTransform = true
  LinkedObject = -> Part002 [Body002.Pocket005.Face2]
  _Parent = -> Elements001
